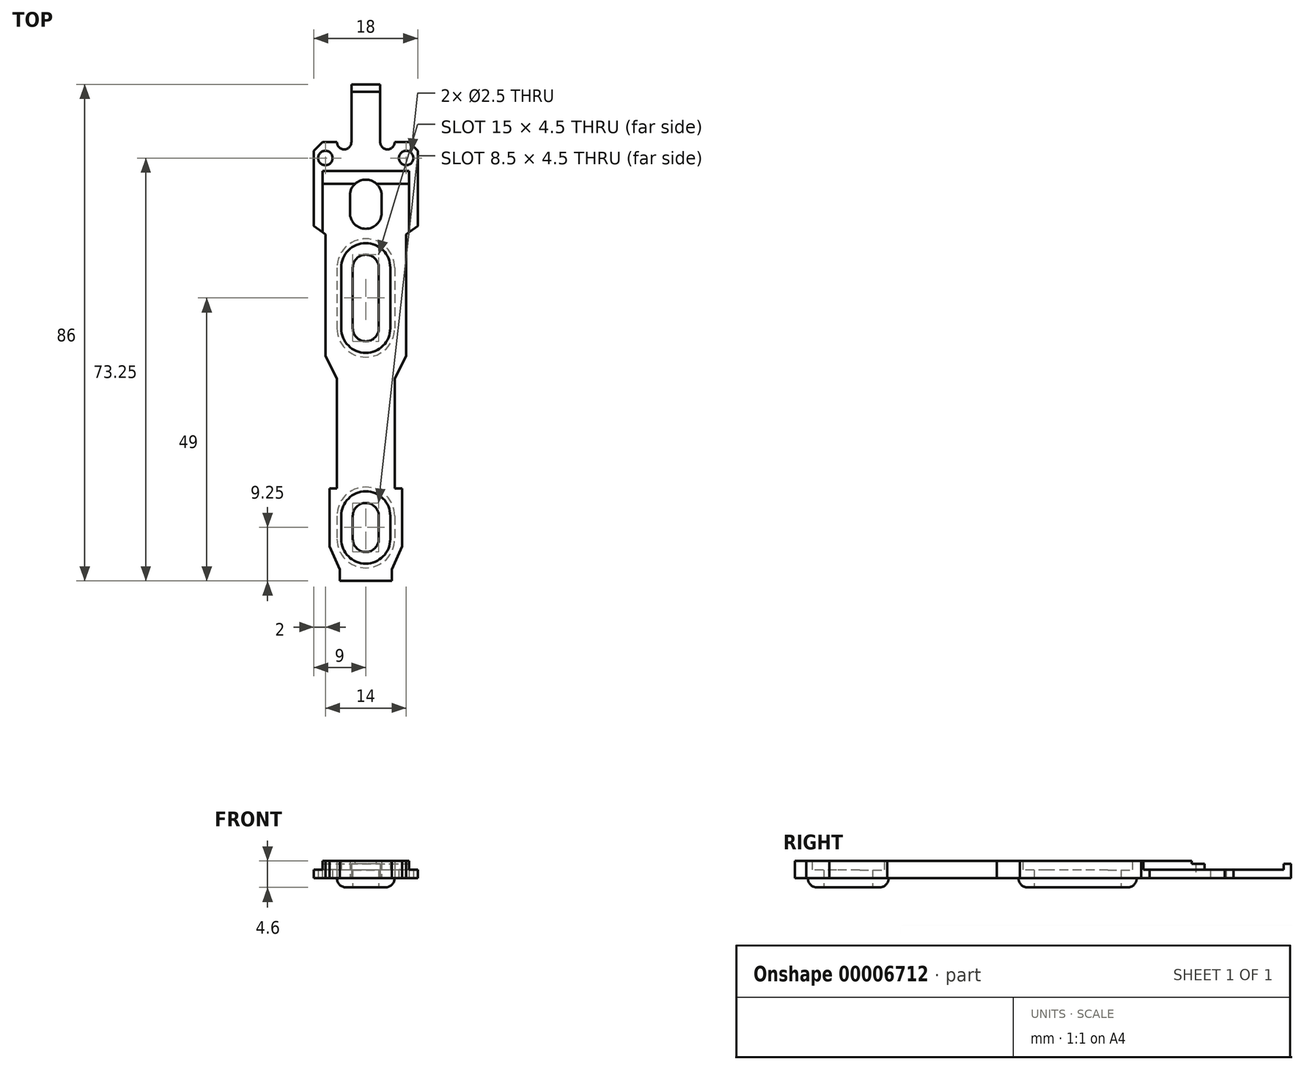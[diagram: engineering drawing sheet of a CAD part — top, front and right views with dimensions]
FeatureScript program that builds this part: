
annotation { "Feature Type Name" : "Feature", "Feature Type Description" : "" }
export const myFeature = defineFeature(function(context is Context, id is Id, definition is map)
    precondition{}
    {
        {
            var Q0;
            Q0=qCreatedBy(makeId("Top.planeOp"),FACE);
            var sketch = newSketch(context, id + "F0", { "sketchPlane" : qUnion([Q0])});
            skLineSegment(sketch, "E0", {"start": v(-2.5, 0) * mm, "end": v(-5, 0) * mm, "construction": true});
            skLineSegment(sketch, "E1", {"start": v(-9, 0) * mm, "end": v(-9, -14.5) * mm});
            skLineSegment(sketch, "E2", {"start": v(-9, -14.5) * mm, "end": v(-7, -16) * mm});
            skLineSegment(sketch, "E3", {"start": v(-7, -16) * mm, "end": v(-7, -37) * mm});
            skLineSegment(sketch, "E4", {"start": v(-7, -37) * mm, "end": v(-5, -41) * mm});
            skLineSegment(sketch, "E5", {"start": v(-5, -41) * mm, "end": v(-5, -60) * mm});
            skLineSegment(sketch, "E6", {"start": v(-5, -60) * mm, "end": v(-6.3, -60) * mm});
            skLineSegment(sketch, "E7", {"start": v(-6.3, -60) * mm, "end": v(-6.3, -70) * mm});
            skLineSegment(sketch, "E8", {"start": v(-6.3, -70) * mm, "end": v(-4.5, -74) * mm});
            skLineSegment(sketch, "E9", {"start": v(-4.5, -74) * mm, "end": v(0, -74) * mm});
            skLineSegment(sketch, "E10", {"start": v(0, 10) * mm, "end": v(-2.5, 10) * mm});
            skLineSegment(sketch, "E11", {"start": v(-2.5, 10) * mm, "end": v(-2.5, 0) * mm});
            skLineSegment(sketch, "E12", {"start": v(-5, 0) * mm, "end": v(-9, 0) * mm});
            skArc(sketch, "E13", {"start": v(-5, 0) * mm, "mid": v(-3.75, -1.25) * mm, "end": v(-2.5, 0) * mm});
            skArc(sketch, "E14", {"start": v(-2.5, 0) * mm, "mid": v(-3.75, 1.25) * mm, "end": v(-5, 0) * mm, "construction": true});
            skLineSegment(sketch, "E15", {"start": v(0, -6.5) * mm, "end": v(0, -6.5) * mm});
            skLineSegment(sketch, "E16", {"start": v(-2.75, -9.25) * mm, "end": v(-2.75, -12.25) * mm});
            skLineSegment(sketch, "E17", {"start": v(0, -15) * mm, "end": v(0, -15) * mm});
            skPoint(sketch, "E18.visualSharp", {"position": v(-2.75, -6.5) * mm});
            skArc(sketch, "E18.filletArc", {"start": v(0, -6.5) * mm, "mid": v(-1.94, -7.3) * mm, "end": v(-2.75, -9.25) * mm});
            skPoint(sketch, "E19.visualSharp", {"position": v(-2.75, -15) * mm});
            skArc(sketch, "E19.filletArc", {"start": v(-2.75, -12.25) * mm, "mid": v(-1.94, -14.2) * mm, "end": v(0, -15) * mm});
            skLineSegment(sketch, "E20", {"start": v(0, -19.5) * mm, "end": v(0, -19.5) * mm});
            skLineSegment(sketch, "E21", {"start": v(-2.25, -21.75) * mm, "end": v(-2.25, -32.25) * mm});
            skLineSegment(sketch, "E22", {"start": v(0, -34.5) * mm, "end": v(0, -34.5) * mm});
            skPoint(sketch, "E23.visualSharp", {"position": v(-2.25, -19.5) * mm});
            skArc(sketch, "E23.filletArc", {"start": v(0, -19.5) * mm, "mid": v(-1.6, -20.16) * mm, "end": v(-2.25, -21.75) * mm});
            skPoint(sketch, "E24.visualSharp", {"position": v(-2.25, -34.5) * mm});
            skArc(sketch, "E24.filletArc", {"start": v(-2.25, -32.25) * mm, "mid": v(-1.6, -33.84) * mm, "end": v(0, -34.5) * mm});
            skLineSegment(sketch, "E25", {"start": v(0, -62.5) * mm, "end": v(0, -62.5) * mm});
            skLineSegment(sketch, "E26", {"start": v(-2.25, -64.75) * mm, "end": v(-2.25, -68.75) * mm});
            skLineSegment(sketch, "E27", {"start": v(0, -71) * mm, "end": v(0, -71) * mm});
            skPoint(sketch, "E28.visualSharp", {"position": v(-2.25, -62.5) * mm});
            skArc(sketch, "E28.filletArc", {"start": v(0, -62.5) * mm, "mid": v(-1.6, -63.16) * mm, "end": v(-2.25, -64.75) * mm});
            skPoint(sketch, "E29.visualSharp", {"position": v(-2.25, -71) * mm});
            skArc(sketch, "E29.filletArc", {"start": v(-2.25, -68.75) * mm, "mid": v(-1.6, -70.34) * mm, "end": v(0, -71) * mm});
            skLineSegment(sketch, "E30.0.MirrorCS", {"start": v(2.5, 0) * mm, "end": v(5, 0) * mm, "construction": true});
            skArc(sketch, "E30.1.MirrorCS", {"start": v(2.5, 0) * mm, "mid": v(3.75, 1.25) * mm, "end": v(5, 0) * mm, "construction": true});
            skPoint(sketch, "E30.2.MirrorP", {"position": v(2.25, -71) * mm});
            skLineSegment(sketch, "E30.3.MirrorCS", {"start": v(4.5, -74) * mm, "end": v(0, -74) * mm});
            skLineSegment(sketch, "E30.4.MirrorCS", {"start": v(6.3, -60) * mm, "end": v(6.3, -70) * mm});
            skPoint(sketch, "E30.5.MirrorP", {"position": v(2.75, -15) * mm});
            skLineSegment(sketch, "E30.6.MirrorCS", {"start": v(2.25, -21.75) * mm, "end": v(2.25, -32.25) * mm});
            skLineSegment(sketch, "E30.7.MirrorCS", {"start": v(2.25, -64.75) * mm, "end": v(2.25, -68.75) * mm});
            skLineSegment(sketch, "E30.8.MirrorCS", {"start": v(2.75, -9.25) * mm, "end": v(2.75, -12.25) * mm});
            skArc(sketch, "E30.9.MirrorCS", {"start": v(2.25, -32.25) * mm, "mid": v(1.6, -33.84) * mm, "end": v(0, -34.5) * mm});
            skLineSegment(sketch, "E30.10.MirrorCS", {"start": v(6.3, -70) * mm, "end": v(4.5, -74) * mm});
            skArc(sketch, "E30.12.MirrorCS", {"start": v(2.75, -12.25) * mm, "mid": v(1.94, -14.2) * mm, "end": v(0, -15) * mm});
            skLineSegment(sketch, "E30.13.MirrorCS", {"start": v(0, 10) * mm, "end": v(2.5, 10) * mm});
            skLineSegment(sketch, "E30.14.MirrorCS", {"start": v(5, 0) * mm, "end": v(9, 0) * mm});
            skPoint(sketch, "E30.15.MirrorP", {"position": v(2.25, -34.5) * mm});
            skArc(sketch, "E30.19.MirrorCS", {"start": v(0, -6.5) * mm, "mid": v(1.94, -7.3) * mm, "end": v(2.75, -9.25) * mm});
            skLineSegment(sketch, "E30.20.MirrorCS", {"start": v(9, 0) * mm, "end": v(9, -14.5) * mm});
            skLineSegment(sketch, "E30.21.MirrorCS", {"start": v(2.5, 10) * mm, "end": v(2.5, 0) * mm});
            skArc(sketch, "E30.22.MirrorCS", {"start": v(0, -62.5) * mm, "mid": v(1.6, -63.16) * mm, "end": v(2.25, -64.75) * mm});
            skPoint(sketch, "E30.23.MirrorP", {"position": v(2.25, -62.5) * mm});
            skPoint(sketch, "E30.24.MirrorP", {"position": v(2.25, -19.5) * mm});
            skArc(sketch, "E30.26.MirrorCS", {"start": v(0, -19.5) * mm, "mid": v(1.6, -20.16) * mm, "end": v(2.25, -21.75) * mm});
            skPoint(sketch, "E30.27.MirrorP", {"position": v(2.75, -6.5) * mm});
            skLineSegment(sketch, "E30.28.MirrorCS", {"start": v(9, -14.5) * mm, "end": v(7, -16) * mm});
            skLineSegment(sketch, "E30.29.MirrorCS", {"start": v(7, -16) * mm, "end": v(7, -37) * mm});
            skArc(sketch, "E30.30.MirrorCS", {"start": v(5, 0) * mm, "mid": v(3.75, -1.25) * mm, "end": v(2.5, 0) * mm});
            skLineSegment(sketch, "E30.32.MirrorCS", {"start": v(5, -41) * mm, "end": v(5, -60) * mm});
            skLineSegment(sketch, "E30.33.MirrorCS", {"start": v(7, -37) * mm, "end": v(5, -41) * mm});
            skArc(sketch, "E30.34.MirrorCS", {"start": v(2.25, -68.75) * mm, "mid": v(1.6, -70.34) * mm, "end": v(0, -71) * mm});
            skLineSegment(sketch, "E30.35.MirrorCS", {"start": v(5, -60) * mm, "end": v(6.3, -60) * mm});
            skCircle(sketch, "E31", {"center": v(-7, -2.75) * mm, "radius": 1.25 * mm});
            skCircle(sketch, "E32.0.MirrorC", {"center": v(7, -2.75) * mm, "radius": 1.25 * mm});
            skArc(sketch, "E33.0", {"start": v(0, -17.5) * mm, "mid": v(-3, -18.74) * mm, "end": v(-4.25, -21.75) * mm});
            skArc(sketch, "E33.1", {"start": v(0, -17.5) * mm, "mid": v(3, -18.74) * mm, "end": v(4.25, -21.75) * mm});
            skLineSegment(sketch, "E33.2", {"start": v(4.25, -21.75) * mm, "end": v(4.25, -32.25) * mm});
            skArc(sketch, "E33.3", {"start": v(4.25, -32.25) * mm, "mid": v(3, -35.26) * mm, "end": v(0, -36.5) * mm});
            skArc(sketch, "E33.4", {"start": v(-4.25, -32.25) * mm, "mid": v(-3, -35.26) * mm, "end": v(0, -36.5) * mm});
            skLineSegment(sketch, "E33.5", {"start": v(-4.25, -21.75) * mm, "end": v(-4.25, -32.25) * mm});
            skArc(sketch, "E34.0", {"start": v(0, -60.5) * mm, "mid": v(-3, -61.74) * mm, "end": v(-4.25, -64.75) * mm});
            skArc(sketch, "E34.1", {"start": v(0, -60.5) * mm, "mid": v(3, -61.74) * mm, "end": v(4.25, -64.75) * mm});
            skLineSegment(sketch, "E34.2", {"start": v(4.25, -64.75) * mm, "end": v(4.25, -68.75) * mm});
            skArc(sketch, "E34.3", {"start": v(4.25, -68.75) * mm, "mid": v(3, -71.76) * mm, "end": v(0, -73) * mm});
            skArc(sketch, "E34.4", {"start": v(-4.25, -68.75) * mm, "mid": v(-3, -71.76) * mm, "end": v(0, -73) * mm});
            skLineSegment(sketch, "E34.5", {"start": v(-4.25, -64.75) * mm, "end": v(-4.25, -68.75) * mm});
            skSolve(sketch);
        }
        {
            var Q0;
            Q0 = qSketchRegion(id + "F0", true);
            extrude(context, id + "F1", {"entities" : qUnion([Q0]), "depth" : 3 * mm});
        }
        {
            var Q0;
            Q0=makeQuery(id+"F1.opExtrude","SWEPT_EDGE",EDGE,{"disambiguationData":[OSD([sQuery(id+"F0.wireOp",EDGE,"E30.14.MirrorCS"),sQuery(id+"F0.wireOp",EDGE,"E30.20.MirrorCS")])]});
            var Q1;
            Q1=makeQuery(id+"F1.opExtrude","SWEPT_EDGE",EDGE,{"disambiguationData":[OSD([sQuery(id+"F0.wireOp",EDGE,"E1"),sQuery(id+"F0.wireOp",EDGE,"E12")])]});
            chamfer(context, id + "F2", {"entities" : qUnion([Q0, Q1]), "chamferType" : ChamferType.OFFSET_ANGLE, "width" : 1.5 * mm, "oppositeDirection" : false, "angle" : 45 * degree, "tangentPropagation" : true});
        }
        {
            var Q0;
            Q0=makeQuery(id+"F0.imprint","IMPRINT",FACE,{"disambiguationData":[TD([[makeQuery(id+"F0.imprint","IMPRINT",EDGE,{"derivedFrom":sQuery(id+"F0.wireOp",EDGE,"E21")}),-1.0]])]});
            var Q1;
            Q1=makeQuery(id+"F0.imprint","IMPRINT",FACE,{"disambiguationData":[TD([[makeQuery(id+"F0.imprint","IMPRINT",EDGE,{"derivedFrom":sQuery(id+"F0.wireOp",EDGE,"E26")}),-1.0]])]});
            extrude(context, id + "F3", {"entities" : qUnion([Q0, Q1]), "operationType" : NewBodyOperationType.ADD, "depth" : 1.4 * mm});
        }
        {
            var Q0;
            Q0=makeQuery(id+"F1.opExtrude","CAP_FACE",FACE,{"disambiguationData":[OSD([sQuery(id+"F0.wireOp",EDGE,"E1"),sQuery(id+"F0.wireOp",EDGE,"E2"),sQuery(id+"F0.wireOp",EDGE,"E3"),sQuery(id+"F0.wireOp",EDGE,"E4"),sQuery(id+"F0.wireOp",EDGE,"E5"),sQuery(id+"F0.wireOp",EDGE,"E6"),sQuery(id+"F0.wireOp",EDGE,"E7"),sQuery(id+"F0.wireOp",EDGE,"E8"),sQuery(id+"F0.wireOp",EDGE,"E9"),sQuery(id+"F0.wireOp",EDGE,"E10"),sQuery(id+"F0.wireOp",EDGE,"E11"),sQuery(id+"F0.wireOp",EDGE,"E12"),sQuery(id+"F0.wireOp",EDGE,"E13"),sQuery(id+"F0.wireOp",EDGE,"E16"),sQuery(id+"F0.wireOp",EDGE,"E18.filletArc"),sQuery(id+"F0.wireOp",EDGE,"E19.filletArc"),sQuery(id+"F0.wireOp",EDGE,"E30.3.MirrorCS"),sQuery(id+"F0.wireOp",EDGE,"E30.4.MirrorCS"),sQuery(id+"F0.wireOp",EDGE,"E30.8.MirrorCS"),sQuery(id+"F0.wireOp",EDGE,"E30.10.MirrorCS"),sQuery(id+"F0.wireOp",EDGE,"E30.12.MirrorCS"),sQuery(id+"F0.wireOp",EDGE,"E30.13.MirrorCS"),sQuery(id+"F0.wireOp",EDGE,"E30.14.MirrorCS"),sQuery(id+"F0.wireOp",EDGE,"E30.19.MirrorCS"),sQuery(id+"F0.wireOp",EDGE,"E30.20.MirrorCS"),sQuery(id+"F0.wireOp",EDGE,"E30.21.MirrorCS"),sQuery(id+"F0.wireOp",EDGE,"E30.28.MirrorCS"),sQuery(id+"F0.wireOp",EDGE,"E30.29.MirrorCS"),sQuery(id+"F0.wireOp",EDGE,"E30.30.MirrorCS"),sQuery(id+"F0.wireOp",EDGE,"E30.32.MirrorCS"),sQuery(id+"F0.wireOp",EDGE,"E30.33.MirrorCS"),sQuery(id+"F0.wireOp",EDGE,"E30.35.MirrorCS"),sQuery(id+"F0.wireOp",EDGE,"E31"),sQuery(id+"F0.wireOp",EDGE,"E32.0.MirrorC"),sQuery(id+"F0.wireOp",EDGE,"E33.0"),sQuery(id+"F0.wireOp",EDGE,"E33.1"),sQuery(id+"F0.wireOp",EDGE,"E33.2"),sQuery(id+"F0.wireOp",EDGE,"E33.3"),sQuery(id+"F0.wireOp",EDGE,"E33.4"),sQuery(id+"F0.wireOp",EDGE,"E33.5"),sQuery(id+"F0.wireOp",EDGE,"E34.0"),sQuery(id+"F0.wireOp",EDGE,"E34.1"),sQuery(id+"F0.wireOp",EDGE,"E34.2"),sQuery(id+"F0.wireOp",EDGE,"E34.3"),sQuery(id+"F0.wireOp",EDGE,"E34.4"),sQuery(id+"F0.wireOp",EDGE,"E34.5")])],"isStart":false});
            var sketch = newSketch(context, id + "F4", { "sketchPlane" : qUnion([Q0])});
            skLineSegment(sketch, "E35.0", {"start": v(-9, -14.5) * mm, "end": v(-7.5, -15.63) * mm});
            skLineSegment(sketch, "E36.0", {"start": v(-9, 0) * mm, "end": v(-9, -14.5) * mm});
            skLineSegment(sketch, "E37", {"start": v(-7.5, -15.63) * mm, "end": v(-7.5, -5) * mm});
            skLineSegment(sketch, "E38", {"start": v(-7.5, -5) * mm, "end": v(0, -5) * mm});
            skLineSegment(sketch, "E39", {"start": v(0, 0) * mm, "end": v(-9, 0) * mm});
            skPoint(sketch, "E40.orphan", {"position": v(-7, -16) * mm});
            skPoint(sketch, "E41.0.MirrorP", {"position": v(7, -16) * mm});
            skLineSegment(sketch, "E41.1.MirrorCS", {"start": v(9, -14.5) * mm, "end": v(7.5, -15.63) * mm});
            skLineSegment(sketch, "E41.2.MirrorCS", {"start": v(9, 0) * mm, "end": v(9, -14.5) * mm});
            skLineSegment(sketch, "E41.3.MirrorCS", {"start": v(7.5, -15.63) * mm, "end": v(7.5, -5) * mm});
            skLineSegment(sketch, "E42.0.MirrorCS", {"start": v(7.5, -5) * mm, "end": v(0, -5) * mm});
            skLineSegment(sketch, "E43.0.MirrorCS", {"start": v(0, 0) * mm, "end": v(9, 0) * mm});
            skLineSegment(sketch, "E44", {"start": v(-2.5, 0) * mm, "end": v(-2.5, 10) * mm});
            skLineSegment(sketch, "E45", {"start": v(-2.5, 10) * mm, "end": v(2.5, 10) * mm});
            skLineSegment(sketch, "E46", {"start": v(2.5, 10) * mm, "end": v(2.5, 0) * mm});
            skSolve(sketch);
        }
        {
            var Q0;
            Q0 = qSketchRegion(id + "F4", true);
            extrude(context, id + "F5", {"entities" : qUnion([Q0]), "operationType" : NewBodyOperationType.REMOVE, "oppositeDirection" : true, "depth" : 1.5 * mm});
        }
        {
            var Q0;
            Q0=makeQuery(id+"F1.opExtrude","CAP_FACE",FACE,{"disambiguationData":[OSD([sQuery(id+"F0.wireOp",EDGE,"E1"),sQuery(id+"F0.wireOp",EDGE,"E2"),sQuery(id+"F0.wireOp",EDGE,"E3"),sQuery(id+"F0.wireOp",EDGE,"E4"),sQuery(id+"F0.wireOp",EDGE,"E5"),sQuery(id+"F0.wireOp",EDGE,"E6"),sQuery(id+"F0.wireOp",EDGE,"E7"),sQuery(id+"F0.wireOp",EDGE,"E8"),sQuery(id+"F0.wireOp",EDGE,"E9"),sQuery(id+"F0.wireOp",EDGE,"E10"),sQuery(id+"F0.wireOp",EDGE,"E11"),sQuery(id+"F0.wireOp",EDGE,"E12"),sQuery(id+"F0.wireOp",EDGE,"E13"),sQuery(id+"F0.wireOp",EDGE,"E16"),sQuery(id+"F0.wireOp",EDGE,"E18.filletArc"),sQuery(id+"F0.wireOp",EDGE,"E19.filletArc"),sQuery(id+"F0.wireOp",EDGE,"E30.3.MirrorCS"),sQuery(id+"F0.wireOp",EDGE,"E30.4.MirrorCS"),sQuery(id+"F0.wireOp",EDGE,"E30.8.MirrorCS"),sQuery(id+"F0.wireOp",EDGE,"E30.10.MirrorCS"),sQuery(id+"F0.wireOp",EDGE,"E30.12.MirrorCS"),sQuery(id+"F0.wireOp",EDGE,"E30.13.MirrorCS"),sQuery(id+"F0.wireOp",EDGE,"E30.14.MirrorCS"),sQuery(id+"F0.wireOp",EDGE,"E30.19.MirrorCS"),sQuery(id+"F0.wireOp",EDGE,"E30.20.MirrorCS"),sQuery(id+"F0.wireOp",EDGE,"E30.21.MirrorCS"),sQuery(id+"F0.wireOp",EDGE,"E30.28.MirrorCS"),sQuery(id+"F0.wireOp",EDGE,"E30.29.MirrorCS"),sQuery(id+"F0.wireOp",EDGE,"E30.30.MirrorCS"),sQuery(id+"F0.wireOp",EDGE,"E30.32.MirrorCS"),sQuery(id+"F0.wireOp",EDGE,"E30.33.MirrorCS"),sQuery(id+"F0.wireOp",EDGE,"E30.35.MirrorCS"),sQuery(id+"F0.wireOp",EDGE,"E31"),sQuery(id+"F0.wireOp",EDGE,"E32.0.MirrorC"),sQuery(id+"F0.wireOp",EDGE,"E33.0"),sQuery(id+"F0.wireOp",EDGE,"E33.1"),sQuery(id+"F0.wireOp",EDGE,"E33.2"),sQuery(id+"F0.wireOp",EDGE,"E33.3"),sQuery(id+"F0.wireOp",EDGE,"E33.4"),sQuery(id+"F0.wireOp",EDGE,"E33.5"),sQuery(id+"F0.wireOp",EDGE,"E34.0"),sQuery(id+"F0.wireOp",EDGE,"E34.1"),sQuery(id+"F0.wireOp",EDGE,"E34.2"),sQuery(id+"F0.wireOp",EDGE,"E34.3"),sQuery(id+"F0.wireOp",EDGE,"E34.4"),sQuery(id+"F0.wireOp",EDGE,"E34.5")])],"isStart":false});
            var sketch = newSketch(context, id + "F6", { "sketchPlane" : qUnion([Q0])});
            skLineSegment(sketch, "E47.bottom", {"start": v(-7.5, -5) * mm, "end": v(7.5, -5) * mm});
            skLineSegment(sketch, "E47.top", {"start": v(-7.5, -7.2) * mm, "end": v(7.5, -7.2) * mm});
            skLineSegment(sketch, "E47.left", {"start": v(-7.5, -5) * mm, "end": v(-7.5, -7.2) * mm});
            skLineSegment(sketch, "E47.right", {"start": v(7.5, -5) * mm, "end": v(7.5, -7.2) * mm});
            skSolve(sketch);
        }
        {
            var Q0;
            Q0=makeQuery(id+"F6.imprint","IMPRINT",FACE,{"disambiguationData":[TD([[makeQuery(id+"F6.imprint","IMPRINT",EDGE,{"derivedFrom":sQuery(id+"F6.wireOp",EDGE,"E47.bottom")}),-1.0]])]});
            extrude(context, id + "F7", {"entities" : qUnion([Q0]), "operationType" : NewBodyOperationType.REMOVE, "oppositeDirection" : true, "depth" : .5 * mm});
        }
        {
            var Q0;
            Q0=makeQuery(id+"F5.boolean.opBoolean","COPY",FACE,{"derivedFrom":makeQuery(id+"F5.opExtrude","CAP_FACE",FACE,{"disambiguationData":[OSD([sQuery(id+"F4.wireOp",EDGE,"E35.0"),sQuery(id+"F4.wireOp",EDGE,"E36.0"),sQuery(id+"F4.wireOp",EDGE,"E37"),sQuery(id+"F4.wireOp",EDGE,"E38"),sQuery(id+"F4.wireOp",EDGE,"E39"),sQuery(id+"F4.wireOp",EDGE,"E41.1.MirrorCS"),sQuery(id+"F4.wireOp",EDGE,"E41.2.MirrorCS"),sQuery(id+"F4.wireOp",EDGE,"E41.3.MirrorCS"),sQuery(id+"F4.wireOp",EDGE,"E42.0.MirrorCS"),sQuery(id+"F4.wireOp",EDGE,"E43.0.MirrorCS"),sQuery(id+"F4.wireOp",EDGE,"E44"),sQuery(id+"F4.wireOp",EDGE,"E45"),sQuery(id+"F4.wireOp",EDGE,"E46")])],"isStart":false})});
            var sketch = newSketch(context, id + "F8", { "sketchPlane" : qUnion([Q0])});
            skLineSegment(sketch, "E48.bottom", {"start": v(-2.5, 10) * mm, "end": v(2.5, 10) * mm});
            skLineSegment(sketch, "E48.top", {"start": v(-2.5, 8.7) * mm, "end": v(2.5, 8.7) * mm});
            skLineSegment(sketch, "E48.left", {"start": v(-2.5, 10) * mm, "end": v(-2.5, 8.7) * mm});
            skLineSegment(sketch, "E48.right", {"start": v(2.5, 10) * mm, "end": v(2.5, 8.7) * mm});
            skSolve(sketch);
        }
        {
            var Q0;
            Q0 = qSketchRegion(id + "F8", true);
            extrude(context, id + "F9", {"entities" : qUnion([Q0]), "operationType" : NewBodyOperationType.ADD, "depth" : 1 * mm});
        }
        {
            var Q0;
            {var subQ0=sQuery(id+"F0.wireOp",EDGE,"E33.0");var subQ1=sQuery(id+"F0.wireOp",EDGE,"E33.1");var subQ2=sQuery(id+"F0.wireOp",EDGE,"E33.2");var subQ3=sQuery(id+"F0.wireOp",EDGE,"E33.3");var subQ4=sQuery(id+"F0.wireOp",EDGE,"E33.4");var subQ5=sQuery(id+"F0.wireOp",EDGE,"E33.5");var subQ6=sQuery(id+"F0.wireOp",EDGE,"E34.0");var subQ7=sQuery(id+"F0.wireOp",EDGE,"E34.1");var subQ8=sQuery(id+"F0.wireOp",EDGE,"E34.2");var subQ9=sQuery(id+"F0.wireOp",EDGE,"E34.3");var subQ10=sQuery(id+"F0.wireOp",EDGE,"E34.4");var subQ11=sQuery(id+"F0.wireOp",EDGE,"E34.5");Q0=makeQuery(id+"F3.boolean.opBoolean","MERGE",FACE,{"derivedFrom":[makeQuery(id+"F1.opExtrude","CAP_FACE",FACE,{"disambiguationData":[OSD([sQuery(id+"F0.wireOp",EDGE,"E1"),sQuery(id+"F0.wireOp",EDGE,"E2"),sQuery(id+"F0.wireOp",EDGE,"E3"),sQuery(id+"F0.wireOp",EDGE,"E4"),sQuery(id+"F0.wireOp",EDGE,"E5"),sQuery(id+"F0.wireOp",EDGE,"E6"),sQuery(id+"F0.wireOp",EDGE,"E7"),sQuery(id+"F0.wireOp",EDGE,"E8"),sQuery(id+"F0.wireOp",EDGE,"E9"),sQuery(id+"F0.wireOp",EDGE,"E10"),sQuery(id+"F0.wireOp",EDGE,"E11"),sQuery(id+"F0.wireOp",EDGE,"E12"),sQuery(id+"F0.wireOp",EDGE,"E13"),sQuery(id+"F0.wireOp",EDGE,"E16"),sQuery(id+"F0.wireOp",EDGE,"E18.filletArc"),sQuery(id+"F0.wireOp",EDGE,"E19.filletArc"),sQuery(id+"F0.wireOp",EDGE,"E30.3.MirrorCS"),sQuery(id+"F0.wireOp",EDGE,"E30.4.MirrorCS"),sQuery(id+"F0.wireOp",EDGE,"E30.8.MirrorCS"),sQuery(id+"F0.wireOp",EDGE,"E30.10.MirrorCS"),sQuery(id+"F0.wireOp",EDGE,"E30.12.MirrorCS"),sQuery(id+"F0.wireOp",EDGE,"E30.13.MirrorCS"),sQuery(id+"F0.wireOp",EDGE,"E30.14.MirrorCS"),sQuery(id+"F0.wireOp",EDGE,"E30.19.MirrorCS"),sQuery(id+"F0.wireOp",EDGE,"E30.20.MirrorCS"),sQuery(id+"F0.wireOp",EDGE,"E30.21.MirrorCS"),sQuery(id+"F0.wireOp",EDGE,"E30.28.MirrorCS"),sQuery(id+"F0.wireOp",EDGE,"E30.29.MirrorCS"),sQuery(id+"F0.wireOp",EDGE,"E30.30.MirrorCS"),sQuery(id+"F0.wireOp",EDGE,"E30.32.MirrorCS"),sQuery(id+"F0.wireOp",EDGE,"E30.33.MirrorCS"),sQuery(id+"F0.wireOp",EDGE,"E30.35.MirrorCS"),sQuery(id+"F0.wireOp",EDGE,"E31"),sQuery(id+"F0.wireOp",EDGE,"E32.0.MirrorC"),subQ0,subQ1,subQ2,subQ3,subQ4,subQ5,subQ6,subQ7,subQ8,subQ9,subQ10,subQ11])],"isStart":true}),makeQuery(id+"F3.opExtrude","CAP_FACE",FACE,{"disambiguationData":[OSD([sQuery(id+"F0.wireOp",EDGE,"E21"),sQuery(id+"F0.wireOp",EDGE,"E23.filletArc"),sQuery(id+"F0.wireOp",EDGE,"E24.filletArc"),sQuery(id+"F0.wireOp",EDGE,"E30.6.MirrorCS"),sQuery(id+"F0.wireOp",EDGE,"E30.9.MirrorCS"),sQuery(id+"F0.wireOp",EDGE,"E30.26.MirrorCS"),subQ0,subQ1,subQ2,subQ3,subQ4,subQ5])],"isStart":true}),makeQuery(id+"F3.opExtrude","CAP_FACE",FACE,{"disambiguationData":[OSD([sQuery(id+"F0.wireOp",EDGE,"E26"),sQuery(id+"F0.wireOp",EDGE,"E28.filletArc"),sQuery(id+"F0.wireOp",EDGE,"E29.filletArc"),sQuery(id+"F0.wireOp",EDGE,"E30.7.MirrorCS"),sQuery(id+"F0.wireOp",EDGE,"E30.22.MirrorCS"),sQuery(id+"F0.wireOp",EDGE,"E30.34.MirrorCS"),subQ6,subQ7,subQ8,subQ9,subQ10,subQ11])],"isStart":true})]});}
            var sketch = newSketch(context, id + "F10", { "sketchPlane" : qUnion([Q0])});
            skLineSegment(sketch, "E49.0", {"start": v(5, 64.75) * mm, "end": v(5, 68.75) * mm});
            skArc(sketch, "E49.1", {"start": v(5, 64.75) * mm, "mid": v(0, 59.75) * mm, "end": v(-5, 64.75) * mm});
            skLineSegment(sketch, "E49.2", {"start": v(-5, 64.75) * mm, "end": v(-5, 68.75) * mm});
            skArc(sketch, "E49.3", {"start": v(5, 68.75) * mm, "mid": v(0, 73.75) * mm, "end": v(-5, 68.75) * mm});
            skArc(sketch, "E50.0", {"start": v(5, 32.25) * mm, "mid": v(0, 37.25) * mm, "end": v(-5, 32.25) * mm});
            skLineSegment(sketch, "E50.1", {"start": v(5, 21.75) * mm, "end": v(5, 32.25) * mm});
            skArc(sketch, "E50.2", {"start": v(5, 21.75) * mm, "mid": v(0, 16.75) * mm, "end": v(-5, 21.75) * mm});
            skLineSegment(sketch, "E50.3", {"start": v(-5, 21.75) * mm, "end": v(-5, 32.25) * mm});
            skArc(sketch, "E51.0", {"start": v(2.25, 32.25) * mm, "mid": v(0, 34.5) * mm, "end": v(-2.25, 32.25) * mm});
            skLineSegment(sketch, "E52.0", {"start": v(2.25, 21.75) * mm, "end": v(2.25, 32.25) * mm});
            skLineSegment(sketch, "E53.0", {"start": v(-2.25, 21.75) * mm, "end": v(-2.25, 32.25) * mm});
            skArc(sketch, "E54.0", {"start": v(2.25, 21.75) * mm, "mid": v(0, 19.5) * mm, "end": v(-2.25, 21.75) * mm});
            skArc(sketch, "E55.0", {"start": v(2.25, 64.75) * mm, "mid": v(0, 62.5) * mm, "end": v(-2.25, 64.75) * mm});
            skLineSegment(sketch, "E56.0", {"start": v(2.25, 64.75) * mm, "end": v(2.25, 68.75) * mm});
            skLineSegment(sketch, "E57.0", {"start": v(-2.25, 64.75) * mm, "end": v(-2.25, 68.75) * mm});
            skArc(sketch, "E58.0", {"start": v(2.25, 68.75) * mm, "mid": v(0, 71) * mm, "end": v(-2.25, 68.75) * mm});
            skSolve(sketch);
        }
        {
            var Q0;
            Q0 = qSketchRegion(id + "F10", true);
            extrude(context, id + "F11", {"entities" : qUnion([Q0]), "operationType" : NewBodyOperationType.ADD, "depth" : 1.6 * mm});
        }
        {
            var Q0;
            Q0=makeQuery(id+"F11.opExtrude","CAP_EDGE",EDGE,{"disambiguationData":[OSD([sQuery(id+"F10.wireOp",EDGE,"E50.3")])],"isStart":false});
            var Q1;
            Q1=makeQuery(id+"F11.opExtrude","CAP_EDGE",EDGE,{"disambiguationData":[OSD([sQuery(id+"F10.wireOp",EDGE,"E49.1")])],"isStart":false});
            fillet(context, id + "F12", {"entities" : qUnion([Q0, Q1]), "radius" : 1.6 * mm, "tangentPropagation" : true, "allowEdgeOverflow" : false});
        }
        {
            var Q0;
            Q0=makeQuery(id+"F1.opExtrude","SWEPT_FACE",FACE,{"disambiguationData":[OSD([sQuery(id+"F0.wireOp",EDGE,"E9"),sQuery(id+"F0.wireOp",EDGE,"E30.3.MirrorCS")])]});
            extrude(context, id + "F13", {"entities" : qUnion([Q0]), "operationType" : NewBodyOperationType.ADD, "depth" : 2 * mm});
        }
    });
